# Revit family: PRD_AR_ShwrFttngsPckg_F5SetForFlushing_ACXT20051
name_source: partatom
category: Specialty Equipment
units: mm (PartAtom-declared; Revit-internal decimal feet)

## family parameters
Always vertical = Yes
Cut with Voids When Loaded = No
Enable Cutting in Views = No
Maintain Annotation Orientation = No
OmniClass Number = 23.65.05.11.11
OmniClass Title = Water Supply Systems
Part Type = Normal
Room Calculation Point = No
Round Connector Dimension = Use Diameter
Shared = No
Work Plane-Based = No

## types (1)
- ACXT2005
    AssetType = Fixed
    BIMObjectName = PRD_AR_ShowerFittingsPackage_F5SetForFlushing_ACXT2005
    BodyMaterial = PRD_AR_Plastic_White
    Category = Pr_40_20_87_75, Shower fittings package
    Default Elevation = 0 mm  [stored 0 ft]
    Description = Set for performing automatic flushing of the cold-water line. Sensor with control electronics and 6 V lithium battery (CR-P2) as well as solenoid valve cartridge. Activated water hygiene flushing (30 seconds), fixed interval of 24 hours and saving of statistical data. With option for parametrisation and communication via optional, bidirectional remote control.
    Export Type to IFC As = IfcSanitaryTerminalType
    Features = Sensor with control electronics and 6 V lithium battery (CR-P2) as well as solenoid valve cartridge.
    IfcExportAs = IfcSanitaryTerminalType
    IfcExportType = USERDEFINED
    Manufacturer = KWC Group Management AG
    ManufacturerName = KWC Group Management AG
    ManufacturerURL = www.kwc-professional.com
    Model = ACXT2005
    ModelNumber = 2030071564
    ModelReference = ACXT2005
    NBSDescription = Shower fittings package
    NBSReference = 45-35-70/330
    Name = F5 Set for flushing ACXT2005
    NominalDepth = 0 mm  [stored 0 ft]
    NominalHeight = 0 mm  [stored 0 ft]
    NominalLength = 0 mm  [stored 0 ft]
    NominalWidth = 0 mm  [stored 0 ft]
    ProductInformation = http://pim.kwc.com
    Size = 0
    Status = New
    Type IFC Predefined Type = USERDEFINED
    URL = www.kwc-professional.com
    Uniclass2015Code = Pr_40_20_87_75
    Uniclass2015Title = Shower fittings package
    Uniclass2015Version = Products v1.36
    Version = 1

note: [stored X ft] marks values corroborated as IEEE doubles in the binary element streams (Revit-internal decimal feet)

## geometry (parser evidence)
native form markers: Sweep x5
no freeform markers — native parametric forms only
